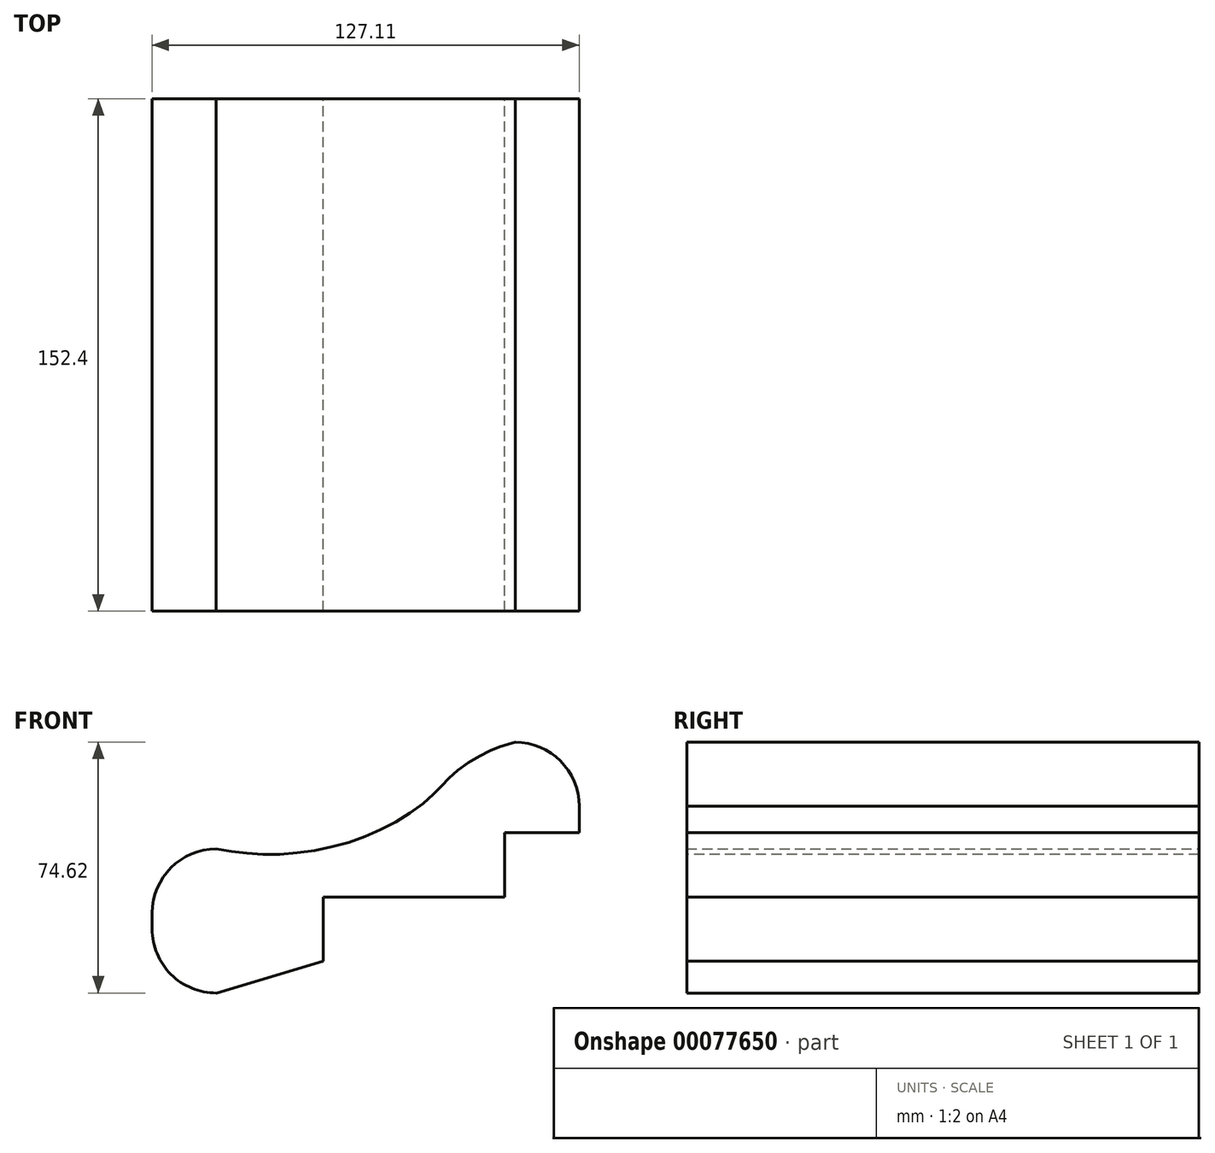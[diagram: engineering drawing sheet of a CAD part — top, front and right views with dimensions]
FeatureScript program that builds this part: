
annotation { "Feature Type Name" : "Feature", "Feature Type Description" : "" }
export const myFeature = defineFeature(function(context is Context, id is Id, definition is map)
    precondition{}
    {
        {
            var Q0;
            Q0=qCreatedBy(makeId("Front.planeOp"),FACE);
            var sketch = newSketch(context, id + "F0", { "sketchPlane" : qUnion([Q0])});
            skLineSegment(sketch, "E0", {"start": v(63.52, 18.25) * mm, "end": v(63.52, 10.34) * mm});
            skLineSegment(sketch, "E1", {"start": v(63.52, 10.34) * mm, "end": v(41.28, 10.34) * mm});
            skLineSegment(sketch, "E2", {"start": v(41.28, 10.34) * mm, "end": v(41.28, -8.73) * mm});
            skLineSegment(sketch, "E3", {"start": v(41.28, -8.73) * mm, "end": v(-12.7, -8.73) * mm});
            skLineSegment(sketch, "E4", {"start": v(-12.7, -8.73) * mm, "end": v(-12.7, -27.78) * mm});
            skLineSegment(sketch, "E5", {"start": v(-12.7, -27.78) * mm, "end": v(-44.4, -37.3) * mm});
            skArc(sketch, "E6", {"start": v(44.46, 37.32) * mm, "mid": v(57.94, 31.74) * mm, "end": v(63.52, 18.26) * mm});
            skLineSegment(sketch, "E7", {"start": v(63.52, 18.26) * mm, "end": v(63.52, 18.25) * mm});
            skArc(sketch, "E8", {"start": v(-63.52, -13.5) * mm, "mid": v(-57.94, -0.02) * mm, "end": v(-44.46, 5.55) * mm});
            skFitSpline(sketch, "E9", {"points": [v(-44.46, 5.55) * mm, v(-28.96, 3.94) * mm, v(-10.02, 6.18) * mm, v(7.36, 12.73) * mm, v(20.08, 21.7) * mm, v(25.66, 27.53) * mm, v(33.93, 33.26) * mm, v(40.75, 36.2) * mm, v(44.46, 37.32) * mm], "startDerivative": vector(103.9, -16.1) * mm, "endDerivative": vector(48.11, 13.47) * mm});
            skArc(sketch, "E10", {"start": v(-44.4, -37.3) * mm, "mid": v(-57.95, -31.76) * mm, "end": v(-63.59, -18.25) * mm});
            skLineSegment(sketch, "E11", {"start": v(-63.59, -18.25) * mm, "end": v(-63.52, -13.5) * mm});
            skSolve(sketch);
        }
        {
            var Q0;
            Q0=makeQuery(id+"F0.imprint","IMPRINT",FACE,{"disambiguationData":[TD([[makeQuery(id+"F0.imprint","IMPRINT",EDGE,{"derivedFrom":sQuery(id+"F0.wireOp",EDGE,"E0")}),-1.0]])]});
            extrude(context, id + "F1", {"entities" : qUnion([Q0]), "depth" : 152.4 * mm});
        }
        {
            var Q0;
            Q0=makeQuery(id+"F1.opExtrude","SWEPT_EDGE",EDGE,{"disambiguationData":[OSD([sQuery(id+"F0.wireOp",EDGE,"E8"),sQuery(id+"F0.wireOp",EDGE,"E11")])]});
            var Q1;
            Q1=makeQuery(id+"F1.opExtrude","SWEPT_EDGE",EDGE,{"disambiguationData":[OSD([sQuery(id+"F0.wireOp",EDGE,"E10"),sQuery(id+"F0.wireOp",EDGE,"E11")])]});
            fillet(context, id + "F2", {"entities" : qUnion([Q0, Q1]), "radius" : 5.08 * mm, "tangentPropagation" : true, "allowEdgeOverflow" : false});
        }
    });
